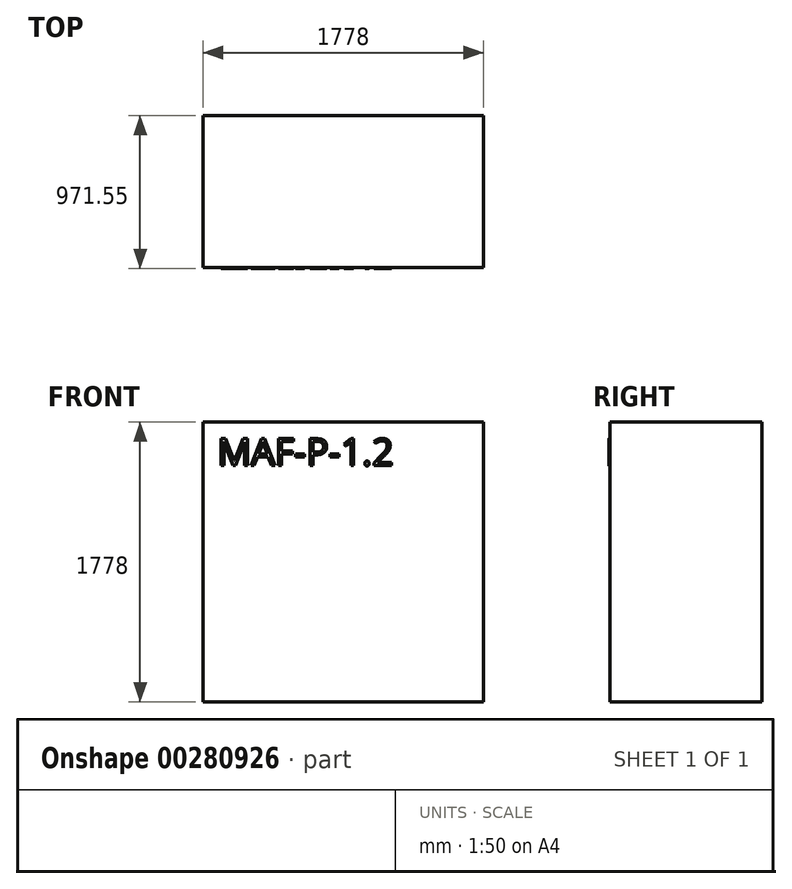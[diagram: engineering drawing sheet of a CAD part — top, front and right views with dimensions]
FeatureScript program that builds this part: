
annotation { "Feature Type Name" : "Feature", "Feature Type Description" : "" }
export const myFeature = defineFeature(function(context is Context, id is Id, definition is map)
    precondition{}
    {
        {
            var Q0;
            Q0=qCreatedBy(makeId("Top.planeOp"),FACE);
            var sketch = newSketch(context, id + "F0", { "sketchPlane" : qUnion([Q0])});
            skLineSegment(sketch, "E0.bottom", {"start": v(0, 0) * mm, "end": v(1778, 0) * mm});
            skLineSegment(sketch, "E0.top", {"start": v(0, 711.2) * mm, "end": v(1778, 711.2) * mm});
            skLineSegment(sketch, "E0.left", {"start": v(0, 0) * mm, "end": v(0, 711.2) * mm});
            skLineSegment(sketch, "E0.right", {"start": v(1778, 0) * mm, "end": v(1778, 711.2) * mm});
            skSolve(sketch);
        }
        {
            var Q0;
            Q0=makeQuery(id+"F0.imprint","IMPRINT",FACE,{"disambiguationData":[TD([[makeQuery(id+"F0.imprint","IMPRINT",EDGE,{"derivedFrom":sQuery(id+"F0.wireOp",EDGE,"E0.bottom")}),1.0]])]});
            extrude(context, id + "F1", {"entities" : qUnion([Q0]), "depth" : 1778 * mm});
        }
        {
            var Q0;
            Q0=makeQuery(id+"F1.opExtrude","SWEPT_FACE",FACE,{"disambiguationData":[OSD([sQuery(id+"F0.wireOp",EDGE,"E0.bottom")])]});
            var sketch = newSketch(context, id + "F2", { "sketchPlane" : qUnion([Q0])});
            skText(sketch, "E1", { "text": "MAF-P-1.2", "fontName": "OpenSans-Regular.ttf"});
            const initialGuessF2  = {"E1": [0.08939, 1.50263, 1, 0, 0.17103]};
            skSetInitialGuess(sketch, initialGuessF2);
            skSolve(sketch);
        }
        {
            var Q0;
            Q0 = qSketchRegion(id + "F2", true);
            extrude(context, id + "F3", {"entities" : qUnion([Q0]), "operationType" : NewBodyOperationType.ADD, "depth" : 6.35 * mm});
        }
        {
            var Q0;
            Q0=makeQuery(id+"F1.opExtrude","SWEPT_FACE",FACE,{"disambiguationData":[OSD([sQuery(id+"F0.wireOp",EDGE,"E0.top")])]});
            extrude(context, id + "F4", {"entities" : qUnion([Q0]), "operationType" : NewBodyOperationType.ADD, "depth" : 254 * mm});
        }
    });
